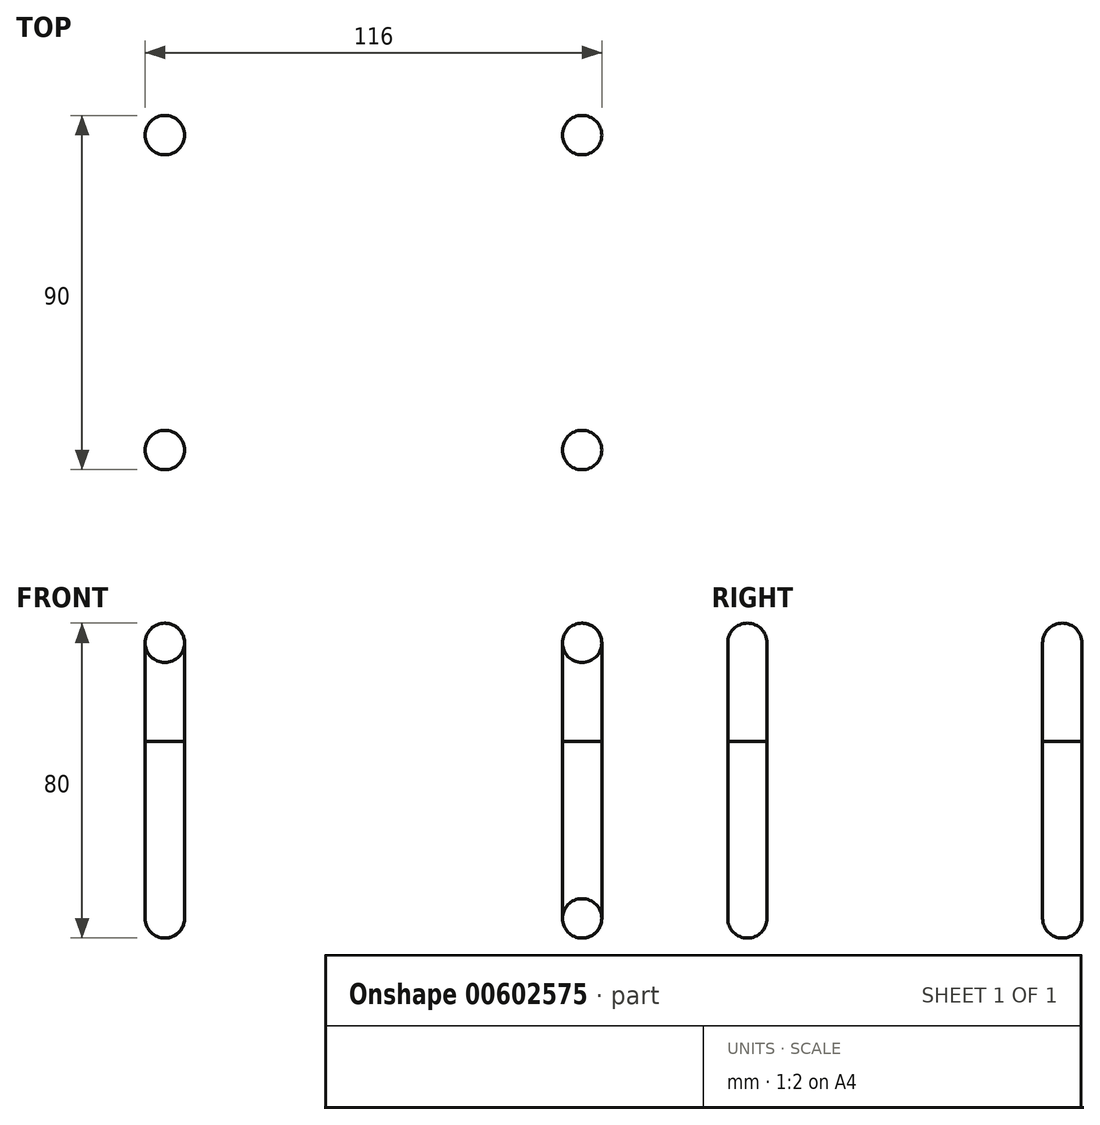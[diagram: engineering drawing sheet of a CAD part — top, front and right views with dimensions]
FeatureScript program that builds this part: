
annotation { "Feature Type Name" : "Feature", "Feature Type Description" : "" }
export const myFeature = defineFeature(function(context is Context, id is Id, definition is map)
    precondition{}
    {
        {
            var Q0;
            Q0=qCreatedBy(makeId("Top.planeOp"),FACE);
            var sketch = newSketch(context, id + "F0", { "sketchPlane" : qUnion([Q0])});
            skCircle(sketch, "E0", {"center": v(-55, 55) * mm, "radius": 5 * mm});
            skCircle(sketch, "E1", {"center": v(51, 55) * mm, "radius": 5 * mm});
            skCircle(sketch, "E2", {"center": v(-55, -25) * mm, "radius": 5 * mm});
            skCircle(sketch, "E3", {"center": v(51, -25) * mm, "radius": 5 * mm});
            skSolve(sketch);
        }
        {
            var Q0;
            Q0=makeQuery(id+"F0.imprint","IMPRINT",FACE,{"disambiguationData":[TD([[makeQuery(id+"F0.imprint","IMPRINT",EDGE,{"derivedFrom":sQuery(id+"F0.wireOp",EDGE,"E0")}),1.0]])]});
            var Q1;
            Q1=makeQuery(id+"F0.imprint","IMPRINT",FACE,{"disambiguationData":[TD([[makeQuery(id+"F0.imprint","IMPRINT",EDGE,{"derivedFrom":sQuery(id+"F0.wireOp",EDGE,"E1")}),1.0]])]});
            var Q2;
            Q2=makeQuery(id+"F0.imprint","IMPRINT",FACE,{"disambiguationData":[TD([[makeQuery(id+"F0.imprint","IMPRINT",EDGE,{"derivedFrom":sQuery(id+"F0.wireOp",EDGE,"E3")}),1.0]])]});
            var Q3;
            Q3=makeQuery(id+"F0.imprint","IMPRINT",FACE,{"disambiguationData":[TD([[makeQuery(id+"F0.imprint","IMPRINT",EDGE,{"derivedFrom":sQuery(id+"F0.wireOp",EDGE,"E2")}),1.0]])]});
            extrude(context, id + "F1", {"entities" : qUnion([Q0, Q1, Q2, Q3]), "oppositeDirection" : true, "depth" : 50 * mm, "offsetDistance" : 25 * mm});
        }
        {
            var Q0;
            Q0=makeQuery(id+"F1.opExtrude","CAP_FACE",FACE,{"disambiguationData":[OSD([sQuery(id+"F0.wireOp",EDGE,"E0")])],"isStart":true});
            var Q1;
            Q1=makeQuery(id+"F1.opExtrude","CAP_FACE",FACE,{"disambiguationData":[OSD([sQuery(id+"F0.wireOp",EDGE,"E1")])],"isStart":true});
            var Q2;
            Q2=makeQuery(id+"F1.opExtrude","CAP_FACE",FACE,{"disambiguationData":[OSD([sQuery(id+"F0.wireOp",EDGE,"E3")])],"isStart":true});
            var Q3;
            Q3=makeQuery(id+"F1.opExtrude","CAP_FACE",FACE,{"disambiguationData":[OSD([sQuery(id+"F0.wireOp",EDGE,"E2")])],"isStart":true});
            extrude(context, id + "F2", {"entities" : qUnion([Q0, Q1, Q2, Q3]), "depth" : 30 * mm, "offsetDistance" : 25 * mm});
        }
        {
            var Q0;
            Q0=makeQuery(id+"F2.opExtrude","CAP_EDGE",EDGE,{"disambiguationData":[OSD([sQuery(id+"F0.wireOp",EDGE,"E0")])],"isStart":false});
            var Q1;
            Q1=makeQuery(id+"F2.opExtrude","CAP_EDGE",EDGE,{"disambiguationData":[OSD([sQuery(id+"F0.wireOp",EDGE,"E1")])],"isStart":false});
            var Q2;
            Q2=makeQuery(id+"F2.opExtrude","CAP_EDGE",EDGE,{"disambiguationData":[OSD([sQuery(id+"F0.wireOp",EDGE,"E3")])],"isStart":false});
            var Q3;
            Q3=makeQuery(id+"F2.opExtrude","CAP_EDGE",EDGE,{"disambiguationData":[OSD([sQuery(id+"F0.wireOp",EDGE,"E2")])],"isStart":false});
            var Q4;
            Q4=makeQuery(id+"F1.opExtrude","CAP_FACE",FACE,{"disambiguationData":[OSD([sQuery(id+"F0.wireOp",EDGE,"E0")])],"isStart":false});
            var Q5;
            Q5=makeQuery(id+"F1.opExtrude","CAP_FACE",FACE,{"disambiguationData":[OSD([sQuery(id+"F0.wireOp",EDGE,"E1")])],"isStart":false});
            var Q6;
            Q6=makeQuery(id+"F1.opExtrude","CAP_FACE",FACE,{"disambiguationData":[OSD([sQuery(id+"F0.wireOp",EDGE,"E3")])],"isStart":false});
            var Q7;
            Q7=makeQuery(id+"F1.opExtrude","CAP_FACE",FACE,{"disambiguationData":[OSD([sQuery(id+"F0.wireOp",EDGE,"E2")])],"isStart":false});
            fillet(context, id + "F3", {"entities" : qUnion([Q0, Q1, Q2, Q3, Q4, Q5, Q6, Q7]), "radius" : 5 * mm, "tangentPropagation" : true, "allowEdgeOverflow" : false});
        }
    });
